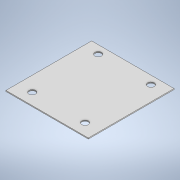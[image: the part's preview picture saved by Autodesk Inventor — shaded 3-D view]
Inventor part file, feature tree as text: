
AUTODESK INVENTOR PART (.ipt)
format: ipt  version: 2022 (Build 260153000, 153)  size: 110,592 bytes
history: native  units: mm
features: extrude x1, sketch x1
ambient origin geometry x8: Origin, YZ Plane, XZ Plane, XY Plane, X Axis, Y Axis, Z Axis, Center Point
bodies: Solid1 (feature_tree)
feature tree (2):
  extrude  "Extrusion1"  Depth=125.0mm
  sketch  "Sketch1"  dims[d0=130.0mm d1=125.0mm d2=10.0mm d3=10.0mm d4=100.0mm d5=10.0mm d6=10.0mm d7=100.0mm d8=80.0mm d9=80.0mm d10=17.5mm d11=22.5mm d12=17.5mm d13=22.5mm d14=1.5mm d15=0.0mm]
